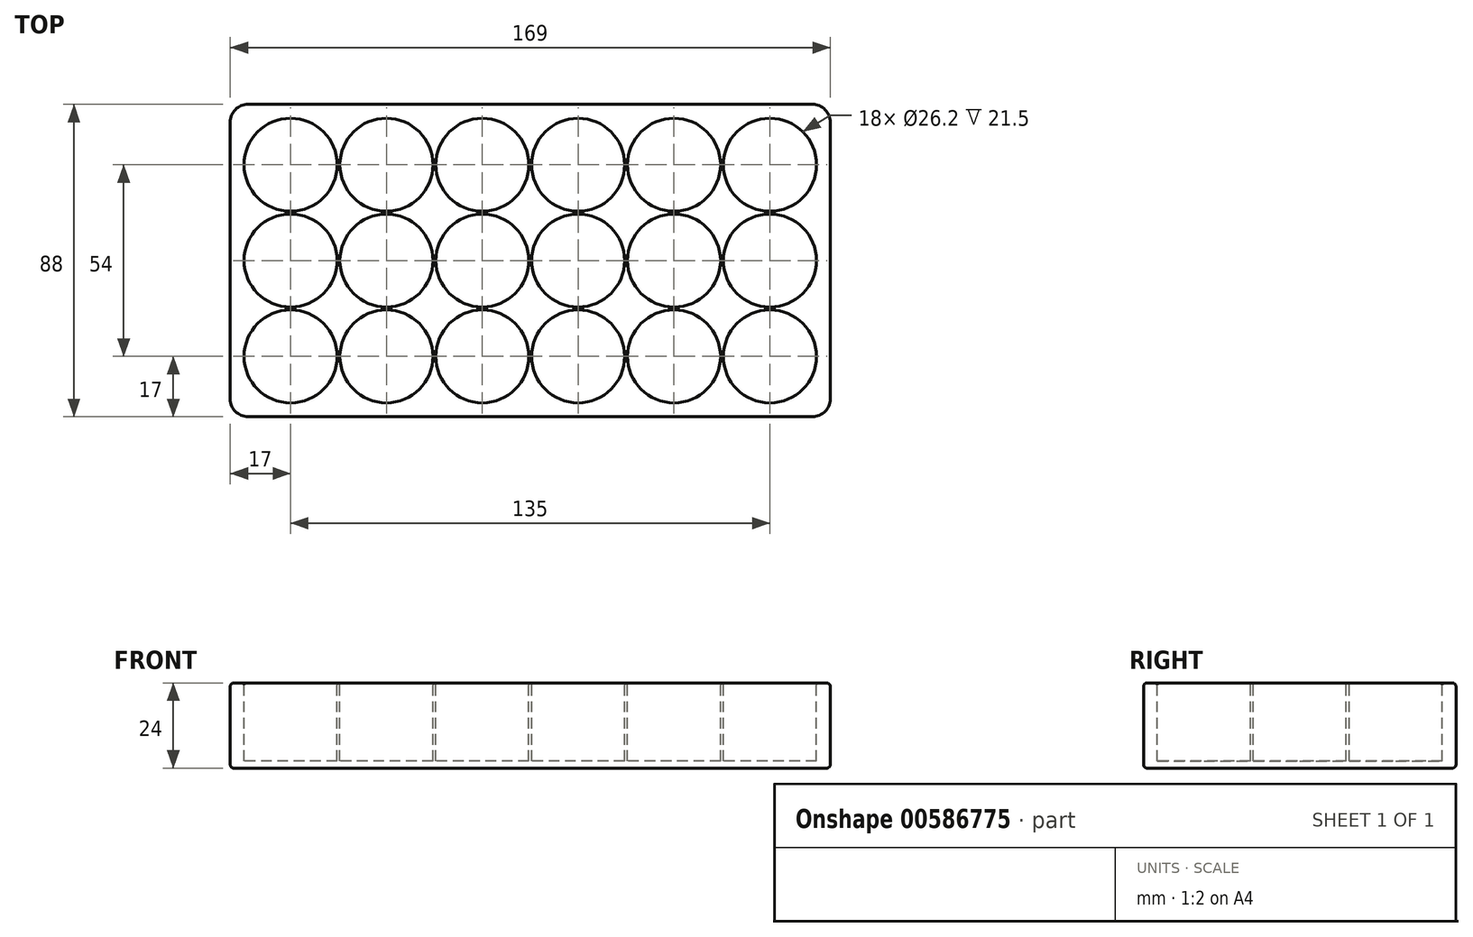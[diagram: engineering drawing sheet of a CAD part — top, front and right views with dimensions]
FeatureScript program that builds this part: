
annotation { "Feature Type Name" : "Feature", "Feature Type Description" : "" }
export const myFeature = defineFeature(function(context is Context, id is Id, definition is map)
    precondition{}
    {
        {
            var Q0;
            Q0=qCreatedBy(makeId("Top.planeOp"),FACE);
            var sketch = newSketch(context, id + "F0", { "sketchPlane" : qUnion([Q0])});
            skPoint(sketch, "E0.middle", {"position": v(0, 0) * mm});
            skCircle(sketch, "E1", {"center": v(0, 0) * mm, "radius": 13.1 * mm});
            skCircle(sketch, "E2.0.1.0", {"center": v(0, 27) * mm, "radius": 13.1 * mm});
            skCircle(sketch, "E2.0.2.0", {"center": v(0, 54) * mm, "radius": 13.1 * mm});
            skCircle(sketch, "E2.1.0.0", {"center": v(27, 0) * mm, "radius": 13.1 * mm});
            skCircle(sketch, "E2.1.1.0", {"center": v(27, 27) * mm, "radius": 13.1 * mm});
            skCircle(sketch, "E2.1.2.0", {"center": v(27, 54) * mm, "radius": 13.1 * mm});
            skCircle(sketch, "E2.2.0.0", {"center": v(54, 0) * mm, "radius": 13.1 * mm});
            skCircle(sketch, "E2.2.1.0", {"center": v(54, 27) * mm, "radius": 13.1 * mm});
            skCircle(sketch, "E2.2.2.0", {"center": v(54, 54) * mm, "radius": 13.1 * mm});
            skCircle(sketch, "E2.3.0.0", {"center": v(81, 0) * mm, "radius": 13.1 * mm});
            skCircle(sketch, "E2.3.1.0", {"center": v(81, 27) * mm, "radius": 13.1 * mm});
            skCircle(sketch, "E2.3.2.0", {"center": v(81, 54) * mm, "radius": 13.1 * mm});
            skCircle(sketch, "E2.4.0.0", {"center": v(108, 0) * mm, "radius": 13.1 * mm});
            skCircle(sketch, "E2.4.1.0", {"center": v(108, 27) * mm, "radius": 13.1 * mm});
            skCircle(sketch, "E2.4.2.0", {"center": v(108, 54) * mm, "radius": 13.1 * mm});
            skCircle(sketch, "E2.5.0.0", {"center": v(135, 0) * mm, "radius": 13.1 * mm});
            skCircle(sketch, "E2.5.1.0", {"center": v(135, 27) * mm, "radius": 13.1 * mm});
            skCircle(sketch, "E2.5.2.0", {"center": v(135, 54) * mm, "radius": 13.1 * mm});
            skLineSegment(sketch, "E2.direction1", {"start": v(0, 0) * mm, "end": v(27, 0) * mm, "construction": true});
            skLineSegment(sketch, "E2.direction2", {"start": v(0, 0) * mm, "end": v(0, 27) * mm, "construction": true});
            skLineSegment(sketch, "E3.bottom", {"start": v(-17, 71) * mm, "end": v(152, 71) * mm});
            skLineSegment(sketch, "E3.top", {"start": v(-17, -17) * mm, "end": v(152, -17) * mm});
            skLineSegment(sketch, "E3.left", {"start": v(-17, 71) * mm, "end": v(-17, -17) * mm});
            skLineSegment(sketch, "E3.right", {"start": v(152, 71) * mm, "end": v(152, -17) * mm});
            skSolve(sketch);
        }
        {
            var Q0;
            Q0=qSketchRegion(id+"F0",true);
            extrude(context, id + "F1", {"entities" : qUnion([Q0]), "oppositeDirection" : true, "depth" : 22 * mm, "offsetDistance" : 25 * mm});
        }
        {
            var Q0;
            Q0=makeQuery(id+"F1.opExtrude","CAP_FACE",FACE,{"disambiguationData":[OSD([sQuery(id+"F0.wireOp",EDGE,"E1"),sQuery(id+"F0.wireOp",EDGE,"E2.0.1.0"),sQuery(id+"F0.wireOp",EDGE,"E2.0.2.0"),sQuery(id+"F0.wireOp",EDGE,"E2.1.0.0"),sQuery(id+"F0.wireOp",EDGE,"E2.1.1.0"),sQuery(id+"F0.wireOp",EDGE,"E2.1.2.0"),sQuery(id+"F0.wireOp",EDGE,"E2.2.0.0"),sQuery(id+"F0.wireOp",EDGE,"E2.2.1.0"),sQuery(id+"F0.wireOp",EDGE,"E2.2.2.0"),sQuery(id+"F0.wireOp",EDGE,"E2.3.0.0"),sQuery(id+"F0.wireOp",EDGE,"E2.3.1.0"),sQuery(id+"F0.wireOp",EDGE,"E2.3.2.0"),sQuery(id+"F0.wireOp",EDGE,"E2.4.0.0"),sQuery(id+"F0.wireOp",EDGE,"E2.4.1.0"),sQuery(id+"F0.wireOp",EDGE,"E2.4.2.0"),sQuery(id+"F0.wireOp",EDGE,"E2.5.0.0"),sQuery(id+"F0.wireOp",EDGE,"E2.5.1.0"),sQuery(id+"F0.wireOp",EDGE,"E2.5.2.0"),sQuery(id+"F0.wireOp",EDGE,"E3.bottom"),sQuery(id+"F0.wireOp",EDGE,"E3.top"),sQuery(id+"F0.wireOp",EDGE,"E3.left"),sQuery(id+"F0.wireOp",EDGE,"E3.right")])],"isStart":false});
            var sketch = newSketch(context, id + "F2", { "sketchPlane" : qUnion([Q0])});
            skLineSegment(sketch, "E4.bottom", {"start": v(152, -71) * mm, "end": v(-17, -71) * mm});
            skLineSegment(sketch, "E4.top", {"start": v(152, 17) * mm, "end": v(-17, 17) * mm});
            skLineSegment(sketch, "E4.left", {"start": v(152, -71) * mm, "end": v(152, 17) * mm});
            skLineSegment(sketch, "E4.right", {"start": v(-17, -71) * mm, "end": v(-17, 17) * mm});
            skSolve(sketch);
        }
        {
            var Q0;
            Q0=qSketchRegion(id+"F2",true);
            extrude(context, id + "F3", {"entities" : qUnion([Q0]), "operationType" : NewBodyOperationType.ADD, "depth" : 2 * mm, "offsetDistance" : 25 * mm});
        }
        {
            var Q0;
            Q0=makeQuery(id+"F1.opExtrude","CAP_EDGE",EDGE,{"disambiguationData":[OSD([sQuery(id+"F0.wireOp",EDGE,"E3.left")])],"isStart":true});
            var Q1;
            Q1=makeQuery(id+"F1.opExtrude","CAP_EDGE",EDGE,{"disambiguationData":[OSD([sQuery(id+"F0.wireOp",EDGE,"E3.bottom")])],"isStart":true});
            var Q2;
            Q2=makeQuery(id+"F1.opExtrude","CAP_EDGE",EDGE,{"disambiguationData":[OSD([sQuery(id+"F0.wireOp",EDGE,"E3.right")])],"isStart":true});
            var Q3;
            Q3=makeQuery(id+"F1.opExtrude","CAP_EDGE",EDGE,{"disambiguationData":[OSD([sQuery(id+"F0.wireOp",EDGE,"E3.top")])],"isStart":true});
            var Q4;
            Q4=makeQuery(id+"F3.opExtrude","CAP_FACE",FACE,{"disambiguationData":[OSD([sQuery(id+"F2.wireOp",EDGE,"E4.bottom"),sQuery(id+"F2.wireOp",EDGE,"E4.top"),sQuery(id+"F2.wireOp",EDGE,"E4.left"),sQuery(id+"F2.wireOp",EDGE,"E4.right")])],"isStart":false});
            fillet(context, id + "F4", {"entities" : qUnion([Q0, Q1, Q2, Q3, Q4]), "radius" : 1 * mm, "tangentPropagation" : true, "allowEdgeOverflow" : false});
        }
        {
            var Q0;
            Q0=makeQuery(id+"F1.opExtrude","CAP_EDGE",EDGE,{"disambiguationData":[OSD([sQuery(id+"F0.wireOp",EDGE,"E2.5.0.0")])],"isStart":true});
            var Q1;
            Q1=makeQuery(id+"F1.opExtrude","CAP_FACE",FACE,{"disambiguationData":[OSD([sQuery(id+"F0.wireOp",EDGE,"E1"),sQuery(id+"F0.wireOp",EDGE,"E2.0.1.0"),sQuery(id+"F0.wireOp",EDGE,"E2.0.2.0"),sQuery(id+"F0.wireOp",EDGE,"E2.1.0.0"),sQuery(id+"F0.wireOp",EDGE,"E2.1.1.0"),sQuery(id+"F0.wireOp",EDGE,"E2.1.2.0"),sQuery(id+"F0.wireOp",EDGE,"E2.2.0.0"),sQuery(id+"F0.wireOp",EDGE,"E2.2.1.0"),sQuery(id+"F0.wireOp",EDGE,"E2.2.2.0"),sQuery(id+"F0.wireOp",EDGE,"E2.3.0.0"),sQuery(id+"F0.wireOp",EDGE,"E2.3.1.0"),sQuery(id+"F0.wireOp",EDGE,"E2.3.2.0"),sQuery(id+"F0.wireOp",EDGE,"E2.4.0.0"),sQuery(id+"F0.wireOp",EDGE,"E2.4.1.0"),sQuery(id+"F0.wireOp",EDGE,"E2.4.2.0"),sQuery(id+"F0.wireOp",EDGE,"E2.5.0.0"),sQuery(id+"F0.wireOp",EDGE,"E2.5.1.0"),sQuery(id+"F0.wireOp",EDGE,"E2.5.2.0"),sQuery(id+"F0.wireOp",EDGE,"E3.bottom"),sQuery(id+"F0.wireOp",EDGE,"E3.top"),sQuery(id+"F0.wireOp",EDGE,"E3.left"),sQuery(id+"F0.wireOp",EDGE,"E3.right")])],"isStart":true});
            fillet(context, id + "F5", {"entities" : qUnion([Q0, Q1]), "radius" : .5 * mm, "tangentPropagation" : true, "allowEdgeOverflow" : false});
        }
        {
            var Q0;
            Q0=makeQuery(id+"F3.boolean.opBoolean","MERGE",EDGE,{"derivedFrom":[makeQuery(id+"F1.opExtrude","SWEPT_EDGE",EDGE,{"disambiguationData":[OSD([sQuery(id+"F0.wireOp",EDGE,"E3.bottom"),sQuery(id+"F0.wireOp",EDGE,"E3.left")])]}),makeQuery(id+"F3.opExtrude","SWEPT_EDGE",EDGE,{"disambiguationData":[OSD([sQuery(id+"F2.wireOp",EDGE,"E4.bottom"),sQuery(id+"F2.wireOp",EDGE,"E4.right")])]})]});
            var Q1;
            Q1=makeQuery(id+"F3.boolean.opBoolean","MERGE",EDGE,{"derivedFrom":[makeQuery(id+"F1.opExtrude","SWEPT_EDGE",EDGE,{"disambiguationData":[OSD([sQuery(id+"F0.wireOp",EDGE,"E3.top"),sQuery(id+"F0.wireOp",EDGE,"E3.left")])]}),makeQuery(id+"F3.opExtrude","SWEPT_EDGE",EDGE,{"disambiguationData":[OSD([sQuery(id+"F2.wireOp",EDGE,"E4.top"),sQuery(id+"F2.wireOp",EDGE,"E4.right")])]})]});
            var Q2;
            Q2=makeQuery(id+"F3.boolean.opBoolean","MERGE",EDGE,{"derivedFrom":[makeQuery(id+"F1.opExtrude","SWEPT_EDGE",EDGE,{"disambiguationData":[OSD([sQuery(id+"F0.wireOp",EDGE,"E3.bottom"),sQuery(id+"F0.wireOp",EDGE,"E3.right")])]}),makeQuery(id+"F3.opExtrude","SWEPT_EDGE",EDGE,{"disambiguationData":[OSD([sQuery(id+"F2.wireOp",EDGE,"E4.bottom"),sQuery(id+"F2.wireOp",EDGE,"E4.left")])]})]});
            var Q3;
            Q3=makeQuery(id+"F3.boolean.opBoolean","MERGE",EDGE,{"derivedFrom":[makeQuery(id+"F1.opExtrude","SWEPT_EDGE",EDGE,{"disambiguationData":[OSD([sQuery(id+"F0.wireOp",EDGE,"E3.top"),sQuery(id+"F0.wireOp",EDGE,"E3.right")])]}),makeQuery(id+"F3.opExtrude","SWEPT_EDGE",EDGE,{"disambiguationData":[OSD([sQuery(id+"F2.wireOp",EDGE,"E4.top"),sQuery(id+"F2.wireOp",EDGE,"E4.left")])]})]});
            fillet(context, id + "F6", {"entities" : qUnion([Q0, Q1, Q2, Q3]), "radius" : 5 * mm, "tangentPropagation" : true, "allowEdgeOverflow" : false});
        }
    });
